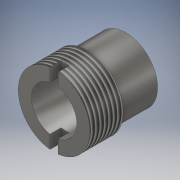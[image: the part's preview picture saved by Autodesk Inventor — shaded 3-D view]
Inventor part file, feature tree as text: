
AUTODESK INVENTOR PART (.ipt)
format: ipt  version: 2017 SP1 (Build 210196100, 196)  size: 141,312 bytes
history: native  units: in
note: dims shown in document units (in); Inventor stores cm internally (conversion verified against a paired STEP export)
features: extrude x3, sketch x3, hole x1, thread x1
ambient origin geometry x8: Origin, YZ Plane, XZ Plane, XY Plane, X Axis, Y Axis, Z Axis, Center Point
bodies: Solid1 (feature_tree)
feature tree (8):
  extrude  "Extrusion1"  TaperAngle=0.0deg  [1 undecoded]
  extrude  "Extrusion2"  Depth=0.8125in
  hole  "Hole1"  [1 undecoded]
  thread  "Thread2"  [1 undecoded]
  extrude  "Extrusion3"  Depth=0.125in
  sketch  "Sketch1"  dims[d0=0.7188in d1=0.0in]
  sketch  "Sketch2"  dims[d2=0.4375in d3=0.0in]
  sketch  "Sketch3"  dims[d18=1.0in d19=1.0in d6=0.5156in d7=0.75in d8=0.375in d9=0.25in d10=0.5635in d11=1.0in d12=0.8108in d15=0.8125in d16=0.375in d17=0.0in d20=0.375in d21=0.0in d22=0.0469in d23=0.45in d24=0.45in d25=0.125in d26=0.0in]
note: 3 required parameter values undecoded (feature->parameter linkage not recoverable at this tier; creation-order binding heuristic only, values carry confidence <= 0.55)
